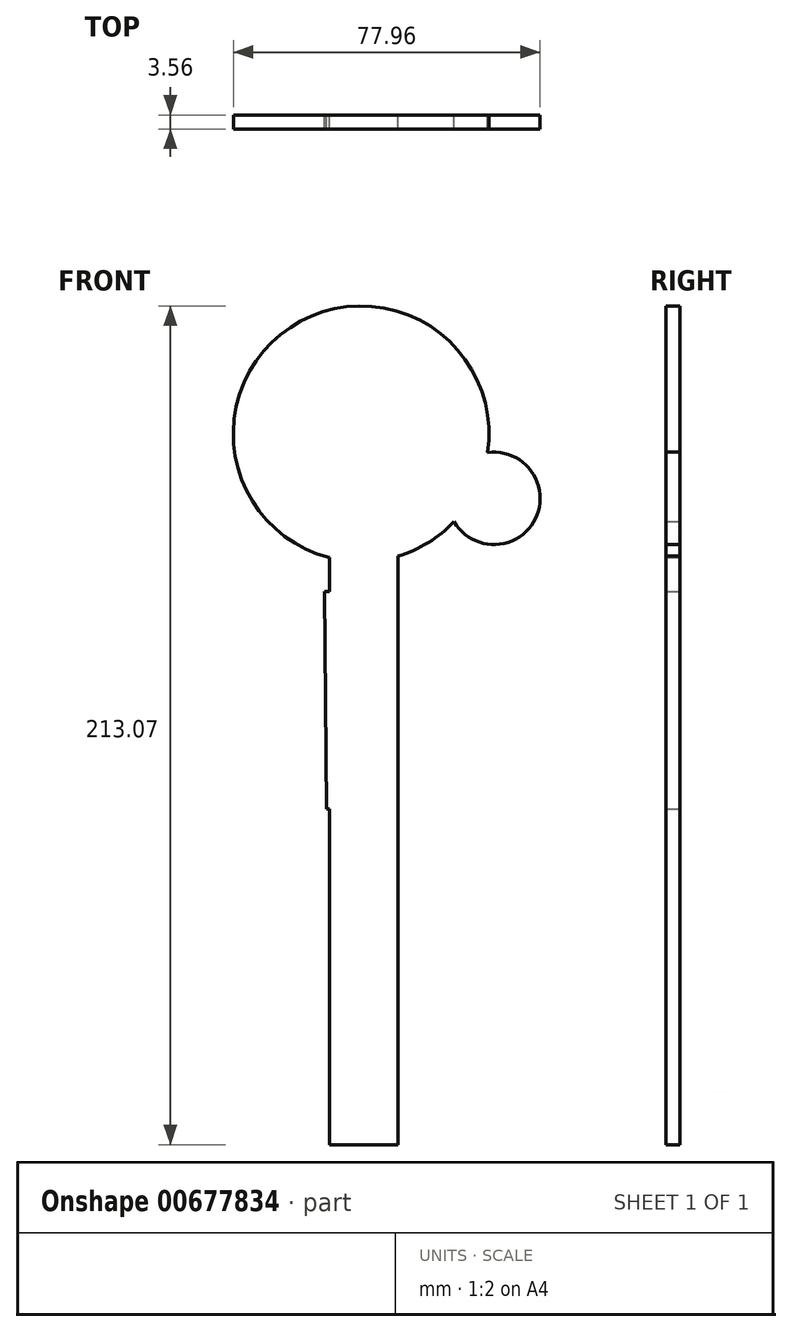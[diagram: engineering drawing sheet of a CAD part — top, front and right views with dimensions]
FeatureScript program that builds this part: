
annotation { "Feature Type Name" : "Feature", "Feature Type Description" : "" }
export const myFeature = defineFeature(function(context is Context, id is Id, definition is map)
    precondition{}
    {
        {
            var Q0;
            Q0=qCreatedBy(makeId("Front.planeOp"),FACE);
            var sketch = newSketch(context, id + "F0", { "sketchPlane" : qUnion([Q0])});
            skArc(sketch, "E0", {"start": v(-5.83, -7.03) * mm, "mid": v(1.87, -3.57) * mm, "end": v(8.42, 1.75) * mm});
            skLineSegment(sketch, "E1.bottom", {"start": v(-24.51, -16) * mm, "end": v(-23.24, -16) * mm});
            skLineSegment(sketch, "E1.top", {"start": v(-24.51, -71.23) * mm, "end": v(-23.24, -71.23) * mm});
            skLineSegment(sketch, "E2.bottom", {"start": v(-5.83, -156.52) * mm, "end": v(-23.24, -156.52) * mm});
            skLineSegment(sketch, "E2.left", {"start": v(-5.83, -156.52) * mm, "end": v(-5.83, -7.03) * mm});
            skLineSegment(sketch, "E2.right", {"start": v(-23.24, -156.52) * mm, "end": v(-23.24, -71.23) * mm});
            skPoint(sketch, "E2.middle", {"position": v(-14.53, -77.7) * mm});
            skLineSegment(sketch, "E3.trimOffspring", {"start": v(-23.24, -16) * mm, "end": v(-23.24, -7.4) * mm});
            skLineSegment(sketch, "E4", {"start": v(-24.51, -16) * mm, "end": v(-23.24, -140.26) * mm});
            skArc(sketch, "E5", {"start": v(8.42, 1.75) * mm, "mid": v(29.12, 2.55) * mm, "end": v(16.95, 19.32) * mm});
            skPoint(sketch, "E6.orphan", {"position": v(-23.24, 1.13) * mm});
            skPoint(sketch, "E7.orphan", {"position": v(-5.83, 1.13) * mm});
            skArc(sketch, "E8.trimOffspring", {"start": v(16.95, 19.32) * mm, "mid": v(-33.16, 51.12) * mm, "end": v(-23.24, -7.4) * mm});
            skSolve(sketch);
        }
        {
            var Q0;
            Q0=makeQuery(id+"F0.imprint","IMPRINT",FACE,{"disambiguationData":[TD([[makeQuery(id+"F0.imprint","IMPRINT",EDGE,{"derivedFrom":sQuery(id+"F0.wireOp",EDGE,"E0")}),1.0]])]});
            extrude(context, id + "F1", {"entities" : qUnion([Q0]), "depth" : 3.56 * mm, "offsetDistance" : 25.4 * mm});
        }
    });
